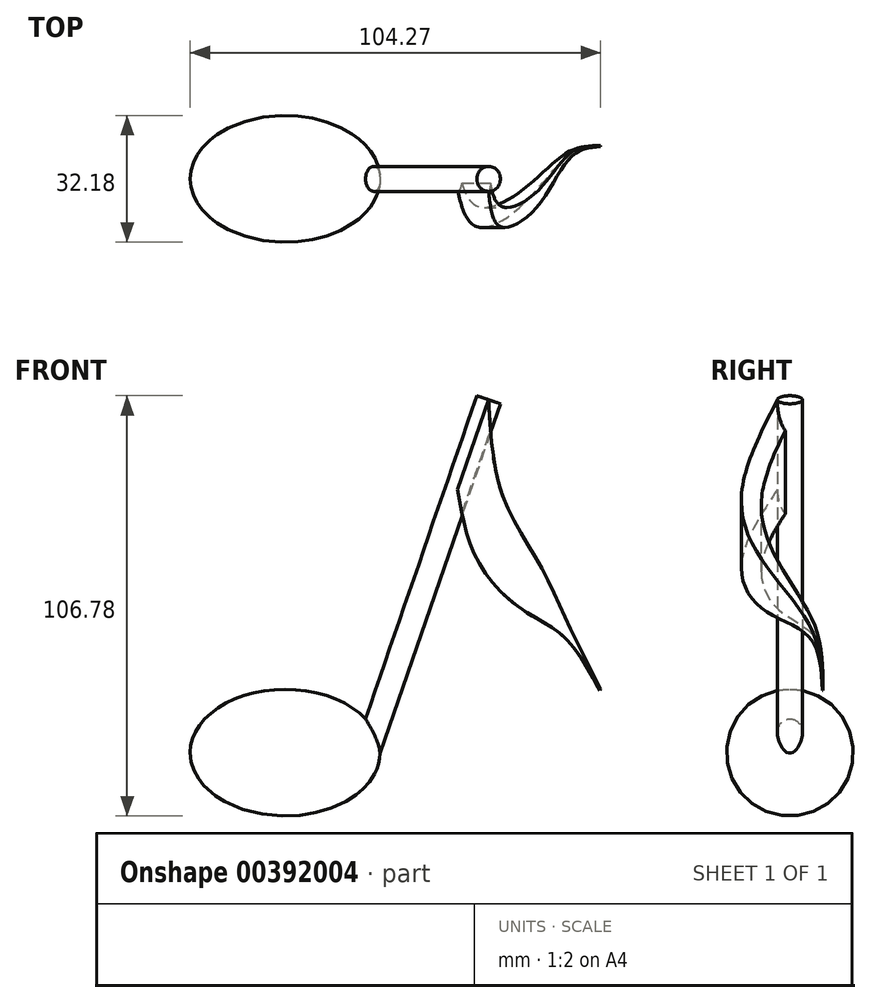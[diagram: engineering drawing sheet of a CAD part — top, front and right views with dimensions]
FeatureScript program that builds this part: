
annotation { "Feature Type Name" : "Feature", "Feature Type Description" : "" }
export const myFeature = defineFeature(function(context is Context, id is Id, definition is map)
    precondition{}
    {
        {
            var Q0;
            Q0=qCreatedBy(makeId("Front.planeOp"),FACE);
            var sketch = newSketch(context, id + "F0", { "sketchPlane" : qUnion([Q0])});
            skEllipticalArc(sketch, "E0", {});
            skLineSegment(sketch, "E1", {"start": v(-48.26, 0) * mm, "end": v(48.26, 0) * mm});
            const initialGuessF0  = {"E0": [0, 0, -1, 0, 0.04826, 0.03217333333333333, 3.141592653589793, 0]};
            skSetInitialGuess(sketch, initialGuessF0);
            skSolve(sketch);
        }
        {
            var Q0;
            Q0=makeQuery(id+"F0.imprint","IMPRINT",FACE,{"disambiguationData":[TD([[makeQuery(id+"F0.imprint","IMPRINT",EDGE,{"derivedFrom":sQuery(id+"F0.wireOp",EDGE,"E0")}),1.0]])]});
            var Q1;
            Q1=sQuery(id+"F0.wireOp",EDGE,"E0");
            var Q2;
            Q2=sQuery(id+"F0.wireOp",EDGE,"E1");
            revolve(context, id + "F1", {"entities" : qUnion([Q0]), "surfaceEntities" : qUnion([Q1]), "axis" : qUnion([Q2]), "revolveType" : RevolveType.FULL});
        }
        {
            var Q0;
            Q0=qCreatedBy(makeId("Right.planeOp"),FACE);
            var sketch = newSketch(context, id + "F2", { "sketchPlane" : qUnion([Q0])});
            skLineSegment(sketch, "E2", {"start": v(-21.06, 0) * mm, "end": v(21.06, 0) * mm, "construction": true});
            skSolve(sketch);
        }
        {
            var Q0;
            Q0=qCreatedBy(makeId("Top.planeOp"),FACE);
            var Q1;
            Q1=sQuery(id+"F2.wireOp",EDGE,"E2");
            cPlane(context, id + "F3", {"entities" : qUnion([Q0, Q1]), "cplaneType" : CPlaneType.LINE_ANGLE, "offset" : 25.4 * mm, "angle" : 19 * degree, "width" : 152.4 * mm, "height" : 152.4 * mm});
        }
        {
            var Q0;
            Q0=qCreatedBy(id+"F3.planeOp",FACE);
            var sketch = newSketch(context, id + "F4", { "sketchPlane" : qUnion([Q0])});
            skCircle(sketch, "E3", {"center": v(39.37, 0) * mm, "radius": 6.35 * mm});
            skSolve(sketch);
        }
        {
            var Q0;
            Q0 = qSketchRegion(id + "F4", true);
            extrude(context, id + "F5", {"entities" : qUnion([Q0]), "operationType" : NewBodyOperationType.ADD, "oppositeDirection" : true, "depth" : 203.2 * mm, "hasSecondDirection" : true, "secondDirectionOppositeDirection" : true, "secondDirectionDepth" : 2.54 * mm});
        }
        {
            var Q0;
            Q0=qCreatedBy(id+"F3.planeOp",FACE);
            var Q1;
            Q1=sQuery(id+"F2.wireOp",EDGE,"E2");
            cPlane(context, id + "F6", {"entities" : qUnion([Q0, Q1]), "cplaneType" : CPlaneType.LINE_ANGLE, "offset" : 25.4 * mm, "angle" : 90 * degree, "width" : 152.4 * mm, "height" : 152.4 * mm});
        }
        {
            var Q0;
            Q0=qCreatedBy(id+"F6.planeOp",FACE);
            cPlane(context, id + "F7", {"entities" : qUnion([Q0]), "cplaneType" : CPlaneType.OFFSET, "offset" : 39.37 * mm, "width" : 152.4 * mm, "height" : 152.4 * mm});
        }
        {
            var Q0;
            Q0=qCreatedBy(id+"F7.planeOp",FACE);
            var sketch = newSketch(context, id + "F8", { "sketchPlane" : qUnion([Q0])});
            skLineSegment(sketch, "E4.bottom", {"start": v(-6.35, 203.2) * mm, "end": v(6.35, 203.2) * mm});
            skLineSegment(sketch, "E4.top", {"start": v(-6.35, 154.94) * mm, "end": v(6.35, 154.94) * mm});
            skLineSegment(sketch, "E4.left", {"start": v(-6.35, 203.2) * mm, "end": v(-6.35, 154.94) * mm});
            skLineSegment(sketch, "E4.right", {"start": v(6.35, 203.2) * mm, "end": v(6.35, 154.94) * mm});
            skPoint(sketch, "E4.middle", {"position": v(0, 179.07) * mm});
            skSolve(sketch);
        }
        {
            var Q0;
            Q0=qCreatedBy(id+"F7.planeOp",FACE);
            cPlane(context, id + "F9", {"entities" : qUnion([Q0]), "cplaneType" : CPlaneType.OFFSET, "offset" : 25.4 * mm, "width" : 152.4 * mm, "height" : 152.4 * mm});
        }
        {
            var Q0;
            Q0=qCreatedBy(id+"F9.planeOp",FACE);
            var sketch = newSketch(context, id + "F10", { "sketchPlane" : qUnion([Q0])});
            skLineSegment(sketch, "E5.bottom", {"start": v(-14.54, 156.18) * mm, "end": v(-24.7, 156.18) * mm});
            skLineSegment(sketch, "E5.top", {"start": v(-14.54, 120.62) * mm, "end": v(-24.7, 120.62) * mm});
            skLineSegment(sketch, "E5.left", {"start": v(-14.54, 156.18) * mm, "end": v(-14.54, 120.62) * mm});
            skLineSegment(sketch, "E5.right", {"start": v(-24.7, 156.18) * mm, "end": v(-24.7, 120.62) * mm});
            skPoint(sketch, "E5.middle", {"position": v(-19.62, 138.4) * mm});
            skSolve(sketch);
        }
        {
            var Q0;
            Q0=qCreatedBy(id+"F9.planeOp",FACE);
            cPlane(context, id + "F11", {"entities" : qUnion([Q0]), "cplaneType" : CPlaneType.OFFSET, "offset" : 25.4 * mm, "width" : 152.4 * mm, "height" : 152.4 * mm});
        }
        {
            var Q0;
            Q0=qCreatedBy(id+"F11.planeOp",FACE);
            var sketch = newSketch(context, id + "F12", { "sketchPlane" : qUnion([Q0])});
            skLineSegment(sketch, "E6.bottom", {"start": v(-13.4, 107.98) * mm, "end": v(-5.77, 107.98) * mm});
            skLineSegment(sketch, "E6.top", {"start": v(-13.4, 133.38) * mm, "end": v(-5.77, 133.38) * mm});
            skLineSegment(sketch, "E6.left", {"start": v(-13.4, 107.98) * mm, "end": v(-13.4, 133.38) * mm});
            skLineSegment(sketch, "E6.right", {"start": v(-5.77, 107.98) * mm, "end": v(-5.77, 133.38) * mm});
            skPoint(sketch, "E6.middle", {"position": v(-9.58, 120.68) * mm});
            skSolve(sketch);
        }
        {
            var Q0;
            Q0=qCreatedBy(id+"F11.planeOp",FACE);
            cPlane(context, id + "F13", {"entities" : qUnion([Q0]), "cplaneType" : CPlaneType.OFFSET, "offset" : 25.4 * mm, "width" : 152.4 * mm, "height" : 152.4 * mm});
        }
        {
            var Q0;
            Q0=qCreatedBy(id+"F13.planeOp",FACE);
            var sketch = newSketch(context, id + "F14", { "sketchPlane" : qUnion([Q0])});
            skLineSegment(sketch, "E7.bottom", {"start": v(12.7, 107.78) * mm, "end": v(10.16, 107.78) * mm});
            skLineSegment(sketch, "E7.top", {"start": v(12.7, 101.43) * mm, "end": v(10.16, 101.43) * mm});
            skLineSegment(sketch, "E7.left", {"start": v(12.7, 107.78) * mm, "end": v(12.7, 101.43) * mm});
            skLineSegment(sketch, "E7.right", {"start": v(10.16, 107.78) * mm, "end": v(10.16, 101.43) * mm});
            skPoint(sketch, "E7.middle", {"position": v(11.43, 104.6) * mm});
            skSolve(sketch);
        }
        {
            var Q0;
            Q0=qCreatedBy(id+"F13.planeOp",FACE);
            cPlane(context, id + "F15", {"entities" : qUnion([Q0]), "cplaneType" : CPlaneType.OFFSET, "offset" : 25.4 * mm, "width" : 152.4 * mm, "height" : 152.4 * mm});
        }
        {
            var Q0;
            Q0=qCreatedBy(id+"F15.planeOp",FACE);
            var sketch = newSketch(context, id + "F16", { "sketchPlane" : qUnion([Q0])});
            skLineSegment(sketch, "E8.bottom", {"start": v(16.41, 82.88) * mm, "end": v(16.9, 82.88) * mm});
            skLineSegment(sketch, "E8.top", {"start": v(16.41, 81.91) * mm, "end": v(16.9, 81.91) * mm});
            skLineSegment(sketch, "E8.left", {"start": v(16.41, 82.88) * mm, "end": v(16.41, 81.91) * mm});
            skLineSegment(sketch, "E8.right", {"start": v(16.9, 82.88) * mm, "end": v(16.9, 81.91) * mm});
            skPoint(sketch, "E8.middle", {"position": v(16.66, 82.4) * mm});
            skSolve(sketch);
        }
        {
            var Q1;
            Q1 = qSketchRegion(id + "F8", true);
            var Q2;
            Q2 = qSketchRegion(id + "F10", true);
            var Q3;
            Q3 = qSketchRegion(id + "F12", true);
            var Q4;
            Q4 = qSketchRegion(id + "F14", true);
            var Q5;
            Q5 = qSketchRegion(id + "F16", true);
            loft(context, id + "F17", {"operationType" : NewBodyOperationType.ADD, "sheetProfilesArray" : [{ "sheetProfileEntities" : qUnion([Q1]) }, { "sheetProfileEntities" : qUnion([Q2]) }, { "sheetProfileEntities" : qUnion([Q3]) }, { "sheetProfileEntities" : qUnion([Q4]) }, { "sheetProfileEntities" : qUnion([Q5]) }]});
        }
        {
            var Q0;
            Q0=makeQuery(id+"F1.opRevolve","SWEPT_BODY",BODY,{"disambiguationData":[OSD([sQuery(id+"F0.wireOp",EDGE,"E0"),sQuery(id+"F0.wireOp",EDGE,"E1")])]});
            var Q1;
            Q1=qCreatedBy(makeId("Origin.pointOp"),VERTEX);
            transform(context, id + "F18", {"entities" : qUnion([Q0]), "transformType" : TransformType.SCALE_UNIFORMLY, "scale" : 0.5, "scalePoint" : qUnion([Q1]), "makeCopy" : false});
        }
    });
